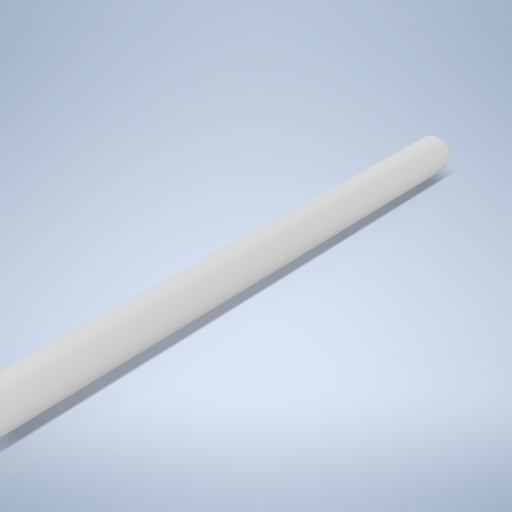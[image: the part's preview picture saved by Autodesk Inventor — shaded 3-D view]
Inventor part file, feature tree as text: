
AUTODESK INVENTOR PART (.ipt)
format: ipt  version: 2024.2 (Build 282272000, 272)  size: 237,568 bytes
history: native  units: mm
features: extrude x1, sketch x1
ambient origin geometry x8: Origin, YZ Plane, XZ Plane, XY Plane, X Axis, Y Axis, Z Axis, Center Point
bodies: Volumenkörper1 (feature_tree)
feature tree (2):
  extrude  "Extrusion1"  Depth=100.0mm TaperAngle=0.0deg
  sketch  "Skizze1"  dims[d0=7.5mm d1=100.0mm d2=0.0mm]
